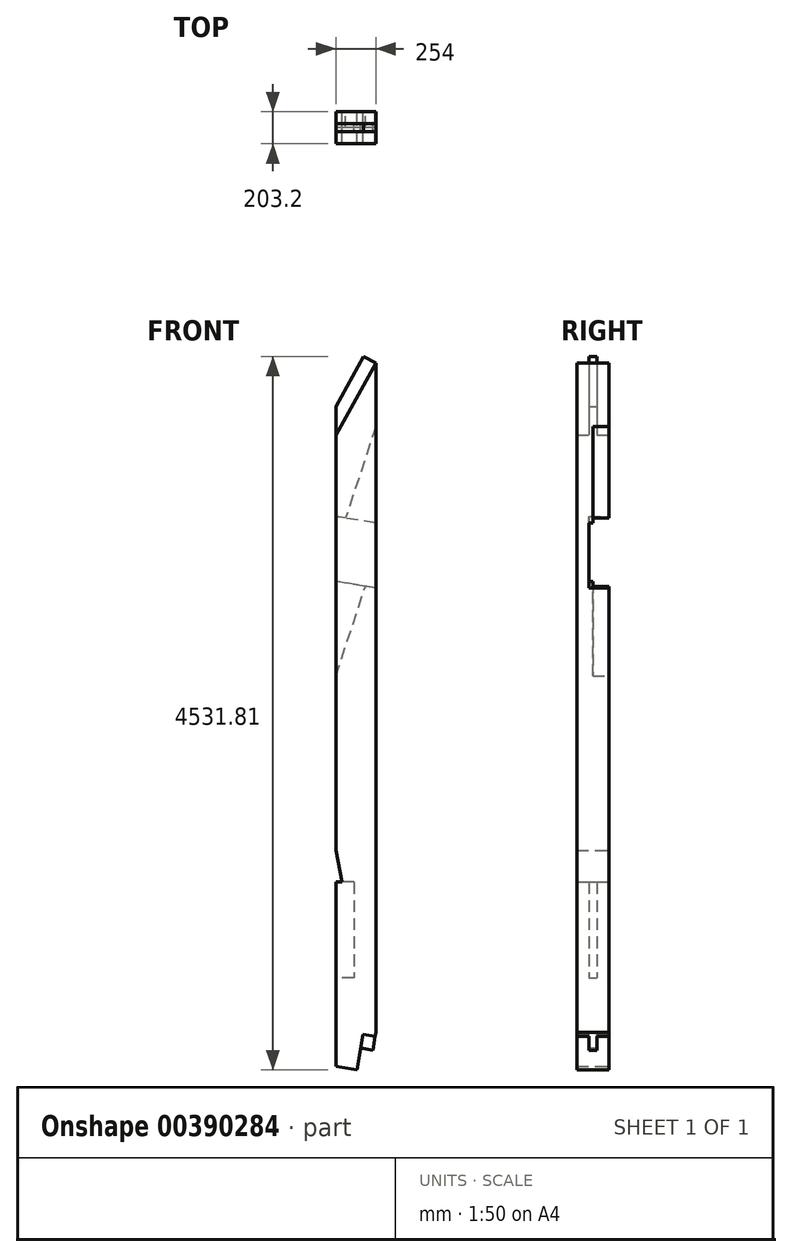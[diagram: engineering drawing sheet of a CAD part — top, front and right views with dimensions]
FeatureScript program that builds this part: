
annotation { "Feature Type Name" : "Feature", "Feature Type Description" : "" }
export const myFeature = defineFeature(function(context is Context, id is Id, definition is map)
    precondition{}
    {
        {
            var Q0;
            Q0=qCreatedBy(makeId("Front.planeOp"),FACE);
            var sketch = newSketch(context, id + "F0", { "sketchPlane" : qUnion([Q0])});
            skLineSegment(sketch, "E0.bottom", {"start": v(-127, 2306.88) * mm, "end": v(127, 2306.88) * mm});
            skLineSegment(sketch, "E0.top", {"start": v(-127, -2306.88) * mm, "end": v(127, -2306.88) * mm});
            skLineSegment(sketch, "E0.left", {"start": v(-127, 2306.88) * mm, "end": v(-127, -2306.88) * mm});
            skLineSegment(sketch, "E0.right", {"start": v(127, 2306.88) * mm, "end": v(127, -2306.88) * mm});
            skPoint(sketch, "E0.middle", {"position": v(0, 0) * mm});
            skLineSegment(sketch, "E1", {"start": v(127, 2227.02) * mm, "end": v(127, 1433.32) * mm});
            skLineSegment(sketch, "E2", {"start": v(127, -2306.88) * mm, "end": v(-127, -2265.12) * mm});
            skLineSegment(sketch, "E3", {"start": v(7.47, -2287.23) * mm, "end": v(127, -1560.17) * mm});
            skLineSegment(sketch, "E4", {"start": v(127, -2049.47) * mm, "end": v(-127, -2007.71) * mm});
            skLineSegment(sketch, "E5", {"start": v(127, -2049.47) * mm, "end": v(122.88, -2074.53) * mm});
            skLineSegment(sketch, "E6", {"start": v(122.88, -2074.53) * mm, "end": v(44.56, -2061.66) * mm});
            skLineSegment(sketch, "E7", {"start": v(122.88, -2074.53) * mm, "end": v(108.46, -2162.26) * mm});
            skLineSegment(sketch, "E8", {"start": v(108.46, -2162.26) * mm, "end": v(30.13, -2149.38) * mm});
            skLineSegment(sketch, "E9", {"start": v(127, 2201.42) * mm, "end": v(-127, 1744.08) * mm});
            skLineSegment(sketch, "E10", {"start": v(-127, -1095.02) * mm, "end": v(-88.96, -1095.02) * mm});
            skLineSegment(sketch, "E11", {"start": v(-88.96, -1095.02) * mm, "end": v(-127, -892.45) * mm});
            skLineSegment(sketch, "E12", {"start": v(127, 2201.42) * mm, "end": v(49.28, 2244.58) * mm});
            skLineSegment(sketch, "E13", {"start": v(49.28, 2244.58) * mm, "end": v(-127, 1927.18) * mm});
            skSolve(sketch);
        }
        {
            var Q0;
            {var subQ0=sQuery(id+"F0.wireOp",EDGE,"E1");var subQ1=sQuery(id+"F0.wireOp",EDGE,"sLSA05CJ-ji3h-L38E-weDl-Nbee3Jkvs57l");var subQ2=makeQuery(id+"F0.imprint","INTERSECT",VERTEX,{"derivedFrom":[subQ1,subQ0]});Q0=makeQuery(id+"F0.imprint","IMPRINT",FACE,{"disambiguationData":[TD([[makeQuery(id+"F0.imprint","IMPRINT",EDGE,{"disambiguationData":[TD([[subQ2,1.0]])],"derivedFrom":subQ1}),-1.0]])]});}
            var Q1;
            {var subQ3=sQuery(id+"F0.wireOp",EDGE,"E2");var subQ5=sQuery(id+"F0.wireOp",EDGE,"E0.left");var subQ6=makeQuery(id+"F0.imprint","INTERSECT",VERTEX,{"derivedFrom":[subQ5,subQ3]});Q1=makeQuery(id+"F0.imprint","IMPRINT",FACE,{"disambiguationData":[TD([[makeQuery(id+"F0.imprint","IMPRINT",EDGE,{"disambiguationData":[TD([[subQ6,1.0]])],"derivedFrom":subQ5}),1.0]])]});}
            var Q2;
            {var subQ4=sQuery(id+"F0.wireOp",EDGE,"E5");Q2=makeQuery(id+"F0.imprint","IMPRINT",FACE,{"disambiguationData":[TD([[makeQuery(id+"F0.imprint","IMPRINT",EDGE,{"derivedFrom":subQ4}),-1.0]])]});}
            var Q3;
            {var subQ0=sQuery(id+"F0.wireOp",EDGE,"E3");var subQ1=sQuery(id+"F0.wireOp",EDGE,"E0.right");var subQ2=makeQuery(id+"F0.imprint","INTERSECT",VERTEX,{"derivedFrom":[subQ1,subQ0]});Q3=makeQuery(id+"F0.imprint","IMPRINT",FACE,{"disambiguationData":[TD([[makeQuery(id+"F0.imprint","IMPRINT",EDGE,{"disambiguationData":[TD([[subQ2,1.0]])],"derivedFrom":subQ0}),-1.0]])]});}
            var Q4;
            {var subQ1=sQuery(id+"F0.wireOp",EDGE,"E0.right");var subQ8=sQuery(id+"F0.wireOp",EDGE,"E3");var subQ10=makeQuery(id+"F0.imprint","INTERSECT",VERTEX,{"derivedFrom":[subQ1,subQ8]});Q4=makeQuery(id+"F0.imprint","IMPRINT",FACE,{"disambiguationData":[TD([[makeQuery(id+"F0.imprint","IMPRINT",EDGE,{"disambiguationData":[TD([[subQ10,1.0]])],"derivedFrom":subQ8}),1.0]])]});}
            var Q5;
            {var subQ0=sQuery(id+"F0.wireOp",EDGE,"AvJj18g5-EUTS-k4jc-6ocs-XMw9zm4LYAZX");var subQ3=sQuery(id+"F0.wireOp",EDGE,"mu8KSUqH-O1Wu-QaL4-81EO-u4Yjg0J5JKGk");var subQ5=makeQuery(id+"F0.imprint","INTERSECT",VERTEX,{"derivedFrom":[subQ0,subQ3]});Q5=makeQuery(id+"F0.imprint","IMPRINT",FACE,{"disambiguationData":[TD([[makeQuery(id+"F0.imprint","IMPRINT",EDGE,{"disambiguationData":[TD([[subQ5,-1.0]])],"derivedFrom":subQ3}),1.0]])]});}
            extrude(context, id + "F1", {"entities" : qUnion([Q0, Q1, Q2, Q3, Q4, Q5]), "endBound" : BoundingType.SYMMETRIC, "depth" : 203.2 * mm});
        }
        {
            var Q0;
            {var subQ5=sQuery(id+"F0.wireOp",EDGE,"PrpMXbKC-m7py-lFAp-eg77-8aCVWW5FYuo4");Q0=makeQuery(id+"F0.imprint","IMPRINT",FACE,{"disambiguationData":[TD([[makeQuery(id+"F0.imprint","IMPRINT",EDGE,{"derivedFrom":subQ5}),-1.0]])]});}
            var Q1;
            {var subQ0=sQuery(id+"F0.wireOp",EDGE,"E6");Q1=makeQuery(id+"F0.imprint","IMPRINT",FACE,{"disambiguationData":[TD([[makeQuery(id+"F0.imprint","IMPRINT",EDGE,{"derivedFrom":subQ0}),1.0]])]});}
            var Q2;
            {var subQ0=sQuery(id+"F0.wireOp",EDGE,"0DDyUR7v-NsTs-4WLy-QZPT-bglCjnublC9u");Q2=makeQuery(id+"F0.imprint","IMPRINT",FACE,{"disambiguationData":[TD([[makeQuery(id+"F0.imprint","IMPRINT",EDGE,{"derivedFrom":subQ0}),-1.0]])]});}
            var Q3;
            Q3=makeQuery(id+"F0.imprint","IMPRINT",FACE,{"disambiguationData":[TD([[makeQuery(id+"F0.imprint","IMPRINT",EDGE,{"derivedFrom":sQuery(id+"F0.wireOp",EDGE,"0DDyUR7v-NsTs-4WLy-QZPT-bglCjnublC9u")}),1.0]])]});
            var Q4;
            {var subQ0=sQuery(id+"F0.wireOp",EDGE,"E1");var subQ5=sQuery(id+"F0.wireOp",EDGE,"sLSA05CJ-ji3h-L38E-weDl-Nbee3Jkvs57l");var subQ6=makeQuery(id+"F0.imprint","INTERSECT",VERTEX,{"derivedFrom":[subQ5,subQ0]});Q4=makeQuery(id+"F0.imprint","IMPRINT",FACE,{"disambiguationData":[TD([[makeQuery(id+"F0.imprint","IMPRINT",EDGE,{"disambiguationData":[TD([[subQ6,1.0]])],"derivedFrom":subQ5}),1.0]])]});}
            var Q5;
            {var subQ0=sQuery(id+"F0.wireOp",EDGE,"E9");Q5=makeQuery(id+"F0.imprint","IMPRINT",FACE,{"disambiguationData":[TD([[makeQuery(id+"F0.imprint","IMPRINT",EDGE,{"derivedFrom":subQ0}),-1.0]])]});}
            extrude(context, id + "F2", {"entities" : qUnion([Q0, Q1, Q2, Q3, Q4, Q5]), "operationType" : NewBodyOperationType.ADD, "endBound" : BoundingType.SYMMETRIC, "depth" : 50.8 * mm});
        }
        {
            var Q0;
            Q0=makeQuery(id+"F1.opExtrude","CAP_FACE",FACE,{"disambiguationData":[OSD([sQuery(id+"F0.wireOp",EDGE,"E0.left"),sQuery(id+"F0.wireOp",EDGE,"E0.right"),sQuery(id+"F0.wireOp",EDGE,"sLSA05CJ-ji3h-L38E-weDl-Nbee3Jkvs57l"),sQuery(id+"F0.wireOp",EDGE,"AvJj18g5-EUTS-k4jc-6ocs-XMw9zm4LYAZX"),sQuery(id+"F0.wireOp",EDGE,"E1"),sQuery(id+"F0.wireOp",EDGE,"E2"),sQuery(id+"F0.wireOp",EDGE,"E3"),sQuery(id+"F0.wireOp",EDGE,"E5"),sQuery(id+"F0.wireOp",EDGE,"E6"),sQuery(id+"F0.wireOp",EDGE,"mu8KSUqH-O1Wu-QaL4-81EO-u4Yjg0J5JKGk")])],"isStart":true});
            var sketch = newSketch(context, id + "F3", { "sketchPlane" : qUnion([Q0])});
            skLineSegment(sketch, "E14", {"start": v(-127, 773.1) * mm, "end": v(127, 773.1) * mm});
            skLineSegment(sketch, "E15", {"start": v(-127, 773.1) * mm, "end": v(127, 814.86) * mm});
            skLineSegment(sketch, "E16", {"start": v(-127, 1184.96) * mm, "end": v(127, 1226.72) * mm});
            skLineSegment(sketch, "E17", {"start": v(127, 1020.8) * mm, "end": v(-127, 979.03) * mm});
            skLineSegment(sketch, "E18", {"start": v(-127, 979.03) * mm, "end": v(127, -565.98) * mm});
            skLineSegment(sketch, "E19", {"start": v(-127, 1799.13) * mm, "end": v(127, 1026.65) * mm});
            skLineSegment(sketch, "E20", {"start": v(127, 213.48) * mm, "end": v(-127, 985.97) * mm});
            skSolve(sketch);
        }
        {
            var Q0;
            {var subQ0=sQuery(id+"F3.wireOp",EDGE,"E18");var subQ1=sQuery(id+"F3.wireOp",EDGE,"E15");var subQ2=makeQuery(id+"F3.imprint","INTERSECT",VERTEX,{"derivedFrom":[subQ1,subQ0]});Q0=makeQuery(id+"F3.imprint","IMPRINT",FACE,{"disambiguationData":[TD([[makeQuery(id+"F3.imprint","IMPRINT",EDGE,{"disambiguationData":[TD([[subQ2,-1.0]])],"derivedFrom":subQ1}),1.0]])]});}
            var Q1;
            {var subQ0=sQuery(id+"F3.wireOp",EDGE,"E18");var subQ1=sQuery(id+"F3.wireOp",EDGE,"E15");var subQ2=makeQuery(id+"F3.imprint","INTERSECT",VERTEX,{"derivedFrom":[subQ1,subQ0]});Q1=makeQuery(id+"F3.imprint","IMPRINT",FACE,{"disambiguationData":[TD([[makeQuery(id+"F3.imprint","IMPRINT",EDGE,{"disambiguationData":[TD([[subQ2,-1.0]])],"derivedFrom":subQ1}),1.0]])]});}
            var Q2;
            {var subQ0=sQuery(id+"F3.wireOp",EDGE,"E15");var subQ3=sQuery(id+"F3.wireOp",EDGE,"E18");var subQ4=makeQuery(id+"F3.imprint","INTERSECT",VERTEX,{"derivedFrom":[subQ0,subQ3]});Q2=makeQuery(id+"F3.imprint","IMPRINT",FACE,{"disambiguationData":[TD([[makeQuery(id+"F3.imprint","IMPRINT",EDGE,{"disambiguationData":[TD([[subQ4,1.0]])],"derivedFrom":subQ0}),1.0]])]});}
            var Q3;
            {var subQ1=makeQuery(id+"F1.opExtrude","CAP_EDGE",EDGE,{"disambiguationData":[OSD([sQuery(id+"F0.wireOp",EDGE,"E0.left")])],"isStart":true});var subQ5=sQuery(id+"F3.wireOp",EDGE,"E15");var subQ6=makeQuery(id+"F3.imprint","INTERSECT",VERTEX,{"derivedFrom":[subQ1,subQ5]});Q3=makeQuery(id+"F3.imprint","IMPRINT",FACE,{"disambiguationData":[TD([[makeQuery(id+"F3.imprint","IMPRINT",EDGE,{"disambiguationData":[TD([[subQ6,1.0]])],"derivedFrom":subQ5}),1.0]])]});}
            var Q4;
            {var subQ0=sQuery(id+"F3.wireOp",EDGE,"E16");var subQ3=sQuery(id+"F3.wireOp",EDGE,"uXVGu14N-Vbd3-mrRb-tT0n-tIGgSwQF9o11");var subQ4=makeQuery(id+"F3.imprint","INTERSECT",VERTEX,{"derivedFrom":[subQ0,subQ3]});Q4=makeQuery(id+"F3.imprint","IMPRINT",FACE,{"disambiguationData":[TD([[makeQuery(id+"F3.imprint","IMPRINT",EDGE,{"disambiguationData":[TD([[subQ4,1.0]])],"derivedFrom":subQ3}),1.0]])]});}
            var Q5;
            {var subQ0=sQuery(id+"F3.wireOp",EDGE,"E16");var subQ1=makeQuery(id+"F1.opExtrude","CAP_EDGE",EDGE,{"disambiguationData":[OSD([sQuery(id+"F0.wireOp",EDGE,"E0.left")])],"isStart":true});var subQ2=makeQuery(id+"F3.imprint","INTERSECT",VERTEX,{"derivedFrom":[subQ1,subQ0]});Q5=makeQuery(id+"F3.imprint","IMPRINT",FACE,{"disambiguationData":[TD([[makeQuery(id+"F3.imprint","IMPRINT",EDGE,{"disambiguationData":[TD([[subQ2,1.0]])],"derivedFrom":subQ0}),-1.0]])]});}
            var Q6;
            {var subQ0=sQuery(id+"F3.wireOp",EDGE,"dBXdCSLG-bP7f-lYZ7-mnlC-Mi42htb4Y9mv");var subQ1=sQuery(id+"F3.wireOp",EDGE,"E15");var subQ2=makeQuery(id+"F3.imprint","INTERSECT",VERTEX,{"derivedFrom":[subQ1,subQ0]});Q6=makeQuery(id+"F3.imprint","IMPRINT",FACE,{"disambiguationData":[TD([[makeQuery(id+"F3.imprint","IMPRINT",EDGE,{"disambiguationData":[TD([[subQ2,-1.0]])],"derivedFrom":subQ1}),1.0]])]});}
            var Q7;
            {var subQ0=sQuery(id+"F3.wireOp",EDGE,"uXVGu14N-Vbd3-mrRb-tT0n-tIGgSwQF9o11");var subQ1=sQuery(id+"F3.wireOp",EDGE,"E16");var subQ2=makeQuery(id+"F3.imprint","INTERSECT",VERTEX,{"derivedFrom":[subQ1,subQ0]});Q7=makeQuery(id+"F3.imprint","IMPRINT",FACE,{"disambiguationData":[TD([[makeQuery(id+"F3.imprint","IMPRINT",EDGE,{"disambiguationData":[TD([[subQ2,-1.0]])],"derivedFrom":subQ1}),-1.0]])]});}
            var Q8;
            {var subQ0=sQuery(id+"F3.wireOp",EDGE,"E17");var subQ3=sQuery(id+"F3.wireOp",EDGE,"E20");var subQ4=makeQuery(id+"F3.imprint","INTERSECT",VERTEX,{"derivedFrom":[subQ0,subQ3]});Q8=makeQuery(id+"F3.imprint","IMPRINT",FACE,{"disambiguationData":[TD([[makeQuery(id+"F3.imprint","IMPRINT",EDGE,{"disambiguationData":[TD([[subQ4,-1.0]])],"derivedFrom":subQ3}),1.0]])]});}
            var Q9;
            {var subQ0=sQuery(id+"F3.wireOp",EDGE,"E17");var subQ4=sQuery(id+"F3.wireOp",EDGE,"uXVGu14N-Vbd3-mrRb-tT0n-tIGgSwQF9o11");var subQ5=makeQuery(id+"F3.imprint","INTERSECT",VERTEX,{"derivedFrom":[subQ0,subQ4]});Q9=makeQuery(id+"F3.imprint","IMPRINT",FACE,{"disambiguationData":[TD([[makeQuery(id+"F3.imprint","IMPRINT",EDGE,{"disambiguationData":[TD([[subQ5,1.0]])],"derivedFrom":subQ0}),1.0]])]});}
            var Q10;
            {var subQ0=sQuery(id+"F3.wireOp",EDGE,"E19");var subQ4=sQuery(id+"F3.wireOp",EDGE,"E16");var subQ5=makeQuery(id+"F3.imprint","INTERSECT",VERTEX,{"derivedFrom":[subQ4,subQ0]});Q10=makeQuery(id+"F3.imprint","IMPRINT",FACE,{"disambiguationData":[TD([[makeQuery(id+"F3.imprint","IMPRINT",EDGE,{"disambiguationData":[TD([[subQ5,1.0]])],"derivedFrom":subQ4}),-1.0]])]});}
            extrude(context, id + "F4", {"entities" : qUnion([Q0, Q1, Q2, Q3, Q4, Q5, Q6, Q7, Q8, Q9, Q10]), "operationType" : NewBodyOperationType.REMOVE, "oppositeDirection" : true, "depth" : 127 * mm});
        }
        {
            var Q0;
            {var subQ0=sQuery(id+"F3.wireOp",EDGE,"E16");var subQ3=sQuery(id+"F3.wireOp",EDGE,"uXVGu14N-Vbd3-mrRb-tT0n-tIGgSwQF9o11");var subQ4=makeQuery(id+"F3.imprint","INTERSECT",VERTEX,{"derivedFrom":[subQ0,subQ3]});Q0=makeQuery(id+"F3.imprint","IMPRINT",FACE,{"disambiguationData":[TD([[makeQuery(id+"F3.imprint","IMPRINT",EDGE,{"disambiguationData":[TD([[subQ4,1.0]])],"derivedFrom":subQ0}),1.0]])]});}
            var Q1;
            {var subQ0=sQuery(id+"F3.wireOp",EDGE,"E14");var subQ1=makeQuery(id+"F1.opExtrude","CAP_EDGE",EDGE,{"disambiguationData":[OSD([sQuery(id+"F0.wireOp",EDGE,"E0.left")])],"isStart":true});var subQ2=makeQuery(id+"F3.imprint","INTERSECT",VERTEX,{"derivedFrom":[subQ1,subQ0]});Q1=makeQuery(id+"F3.imprint","IMPRINT",FACE,{"disambiguationData":[TD([[makeQuery(id+"F3.imprint","IMPRINT",EDGE,{"disambiguationData":[TD([[subQ2,1.0]])],"derivedFrom":subQ0}),-1.0]])]});}
            var Q2;
            {var subQ0=sQuery(id+"F3.wireOp",EDGE,"E14");var subQ1=makeQuery(id+"F1.opExtrude","CAP_EDGE",EDGE,{"disambiguationData":[OSD([sQuery(id+"F0.wireOp",EDGE,"E0.left")])],"isStart":true});var subQ2=makeQuery(id+"F3.imprint","INTERSECT",VERTEX,{"derivedFrom":[subQ1,subQ0]});Q2=makeQuery(id+"F3.imprint","IMPRINT",FACE,{"disambiguationData":[TD([[makeQuery(id+"F3.imprint","IMPRINT",EDGE,{"disambiguationData":[TD([[subQ2,1.0]])],"derivedFrom":subQ0}),1.0]])]});}
            var Q3;
            {var subQ0=sQuery(id+"F3.wireOp",EDGE,"uXVGu14N-Vbd3-mrRb-tT0n-tIGgSwQF9o11");var subQ1=sQuery(id+"F3.wireOp",EDGE,"E16");var subQ2=makeQuery(id+"F3.imprint","INTERSECT",VERTEX,{"derivedFrom":[subQ1,subQ0]});Q3=makeQuery(id+"F3.imprint","IMPRINT",FACE,{"disambiguationData":[TD([[makeQuery(id+"F3.imprint","IMPRINT",EDGE,{"disambiguationData":[TD([[subQ2,-1.0]])],"derivedFrom":subQ1}),1.0]])]});}
            extrude(context, id + "F5", {"entities" : qUnion([Q0, Q1, Q2, Q3]), "operationType" : NewBodyOperationType.REMOVE, "oppositeDirection" : true, "depth" : 101.6 * mm});
        }
        {
            var Q0;
            {var subQ0=sQuery(id+"F0.wireOp",EDGE,"E0.left");var subQ1=makeQuery(id+"F0.imprint","INTERSECT",VERTEX,{"derivedFrom":[subQ0,sQuery(id+"F0.wireOp",EDGE,"E4")]});Q0=makeQuery(id+"F1.opExtrude","SWEPT_FACE",FACE,{"disambiguationData":[OSD([subQ0]),TDD([makeQuery(id+"F0.imprint","IMPRINT",EDGE,{"disambiguationData":[TD([[subQ1,1.0]])],"derivedFrom":subQ0}),makeQuery(id+"F0.imprint","IMPRINT",EDGE,{"disambiguationData":[TD([[makeQuery(id+"F0.imprint","INTERSECT",VERTEX,{"derivedFrom":[subQ0,sQuery(id+"F0.wireOp",EDGE,"E2")]}),1.0]])],"derivedFrom":subQ0})])]});}
            var sketch = newSketch(context, id + "F6", { "sketchPlane" : qUnion([Q0])});
            skLineSegment(sketch, "E21.bottom", {"start": v(25.4, -1095.02) * mm, "end": v(-25.4, -1095.02) * mm});
            skLineSegment(sketch, "E21.top", {"start": v(25.4, -1704.62) * mm, "end": v(-25.4, -1704.62) * mm});
            skLineSegment(sketch, "E21.left", {"start": v(25.4, -1095.02) * mm, "end": v(25.4, -1704.62) * mm});
            skLineSegment(sketch, "E21.right", {"start": v(-25.4, -1095.02) * mm, "end": v(-25.4, -1704.62) * mm});
            skPoint(sketch, "E21.middle", {"position": v(0, -1399.82) * mm});
            skSolve(sketch);
        }
        {
            var Q0;
            Q0=makeQuery(id+"F6.imprint","IMPRINT",FACE,{"disambiguationData":[TD([[makeQuery(id+"F6.imprint","IMPRINT",EDGE,{"derivedFrom":sQuery(id+"F6.wireOp",EDGE,"E21.bottom")}),1.0]])]});
            extrude(context, id + "F7", {"entities" : qUnion([Q0]), "operationType" : NewBodyOperationType.REMOVE, "oppositeDirection" : true, "depth" : 114.3 * mm, "offsetDistance" : 25.4 * mm});
        }
    });
